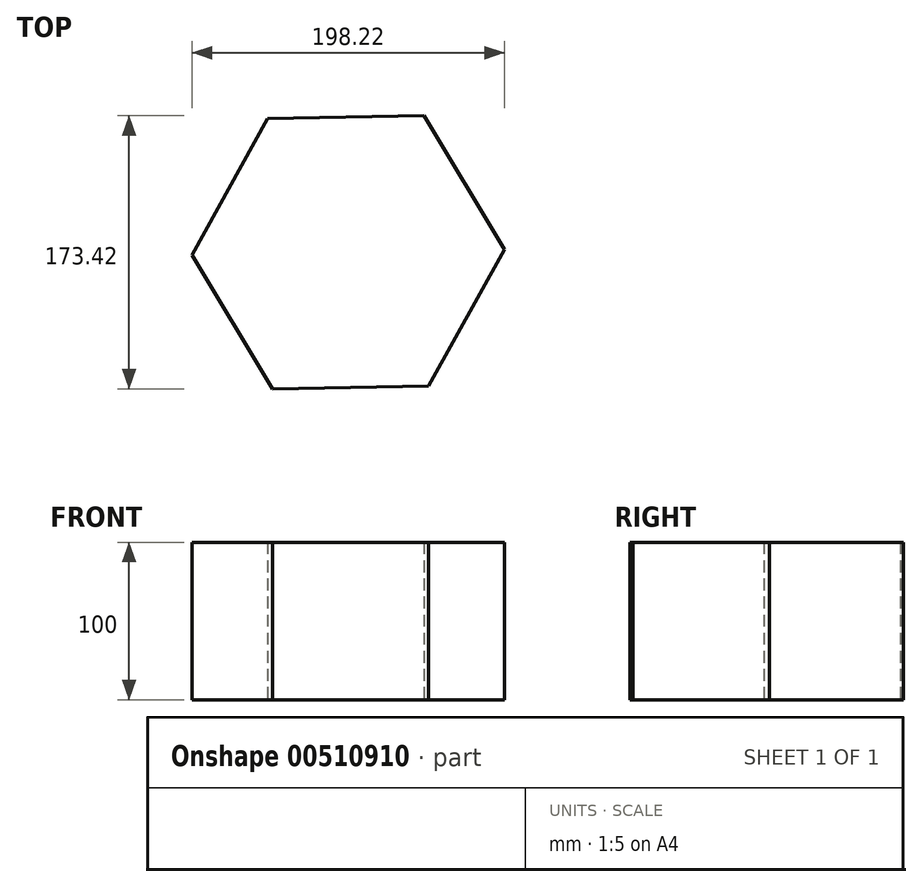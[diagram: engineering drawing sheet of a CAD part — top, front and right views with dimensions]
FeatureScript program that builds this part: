
annotation { "Feature Type Name" : "Feature", "Feature Type Description" : "" }
export const myFeature = defineFeature(function(context is Context, id is Id, definition is map)
    precondition{}
    {
        {
            var Q0;
            Q0=qCreatedBy(makeId("Top.planeOp"),FACE);
            var sketch = newSketch(context, id + "F0", { "sketchPlane" : qUnion([Q0])});
            skCircle(sketch, "E0.cCircle", {"center": v(0, 0) * mm, "radius": 99.13 * mm, "construction": true});
            skLineSegment(sketch, "E0.0", {"start": v(51.07, -84.96) * mm, "end": v(-48.04, -86.7) * mm});
            skLineSegment(sketch, "E0.1", {"start": v(-48.04, -86.7) * mm, "end": v(-99.11, -1.75) * mm});
            skLineSegment(sketch, "E0.2", {"start": v(-99.11, -1.75) * mm, "end": v(-51.07, 84.96) * mm});
            skLineSegment(sketch, "E0.3", {"start": v(-51.07, 84.96) * mm, "end": v(48.04, 86.7) * mm});
            skLineSegment(sketch, "E0.4", {"start": v(48.04, 86.7) * mm, "end": v(99.11, 1.75) * mm});
            skLineSegment(sketch, "E0.5", {"start": v(99.11, 1.75) * mm, "end": v(51.07, -84.96) * mm});
            skSolve(sketch);
        }
        {
            var Q0;
            Q0 = qSketchRegion(id + "F0", true);
            extrude(context, id + "F1", {"entities" : qUnion([Q0]), "depth" : 100 * mm});
        }
    });
